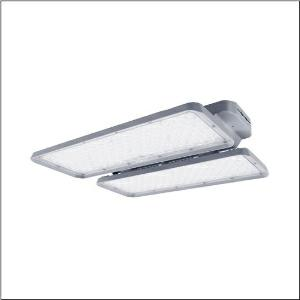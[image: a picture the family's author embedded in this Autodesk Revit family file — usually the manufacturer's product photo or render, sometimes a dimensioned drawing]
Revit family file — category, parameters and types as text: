
# Revit family: highbay_21-l_51hk41db4qca
name_source: partatom
category: Lighting Fixtures
units: mm (PartAtom-declared; Revit-internal decimal feet)

## family parameters
Cut with Voids When Loaded = No
Host = Face
Light Source = No
Part Type = Normal
Room Calculation Point = No
Round Connector Dimension = Use Diameter
Shared = No

## types (1)
- Highbay 21-L (1 x LED, 35600 lm, 200 W, 4000K)
    Apparent Load = 200 VA
    CIE Flux Codes = 87 97 99 100 100
    Color Rendering = 80
    Color Temperature = 4000K
    Default Elevation = 1800 mm
    Description = Highbay 21-L, LED high bay luminaire, primary light control with lens, of PC, light emission: direct distribution, primary light characteristic: symmetric, installation type: suspended mounting, surface-mounted, LED, rated luminous flux: 35.600lm, luminous efficacy: 178lm/W, light colour: 840, colour temperature: 4000K, with terminal, 5-pole, max. 2.5mm², mains connection: 220..240V, AC, 50Hz, rated input power: 200W, housing, of diecast aluminium, coated, grey, length: 471mm, width: 390mm, height: 87mm, protection rating (complete): IP66, insulation class (complete): insulation class I (protective earthing), certification: CE, ENEC, UKCA, protection symbol: D, impact resistance: IK08, permissible operating ambient temperature: -30..+60°C, corresponds to IFS (International Featured Standards) requirements for safety and quality in the food industry, LABS conformity tested according to VDMA 24364:2018-05, packaging unit: 1 piece
    Height = 89 mm
    Lamp = 1 x LED
    Lamp Light Flux = 35600 lm
    Lamp Power = 200 W
    Lamp count = 1
    Length = 471 mm
    Luminous efficacy = 178 lm/W
    Manufacturer = Siteco
    ModVariant = No
    Model = 51HK41DB4QCA
    Mounting Place = Ceiling
    Mounting Type = Pendant
    Number of Poles = 1
    OnlyDefault = Yes
    Power Factor = 1
    Product Name = Highbay 21-L
    Product group = LED high bay luminaire
    ProductGroupID = 903
    Protection Class = Protection class I
    Protection Degree = IP 66
    RLX_Detail_Level = 1
    RLX_Emergency_Light_Flux = 0 lm
    RLX_Emergency_Type = 0
    RLX_Emergency_Type_DB = No
    RlxData = <blob elided: 25429 chars, md5=6c78b5f3>
    Socket = socket
    Standby Power = 0 W
    System Light Flux = 35600 lm
    System Power = 200 W
    Type Comments = Product without accessories
    Type Image = l_1276530.jpg
    URL = http://relux.com
    VarID = ---
    Voltage = 0 V
    Weight = 0.00 kg
    Width = 390 mm

## geometry (parser evidence)
native form markers: Blend x4, Sweep x12
no freeform markers — native parametric forms only
